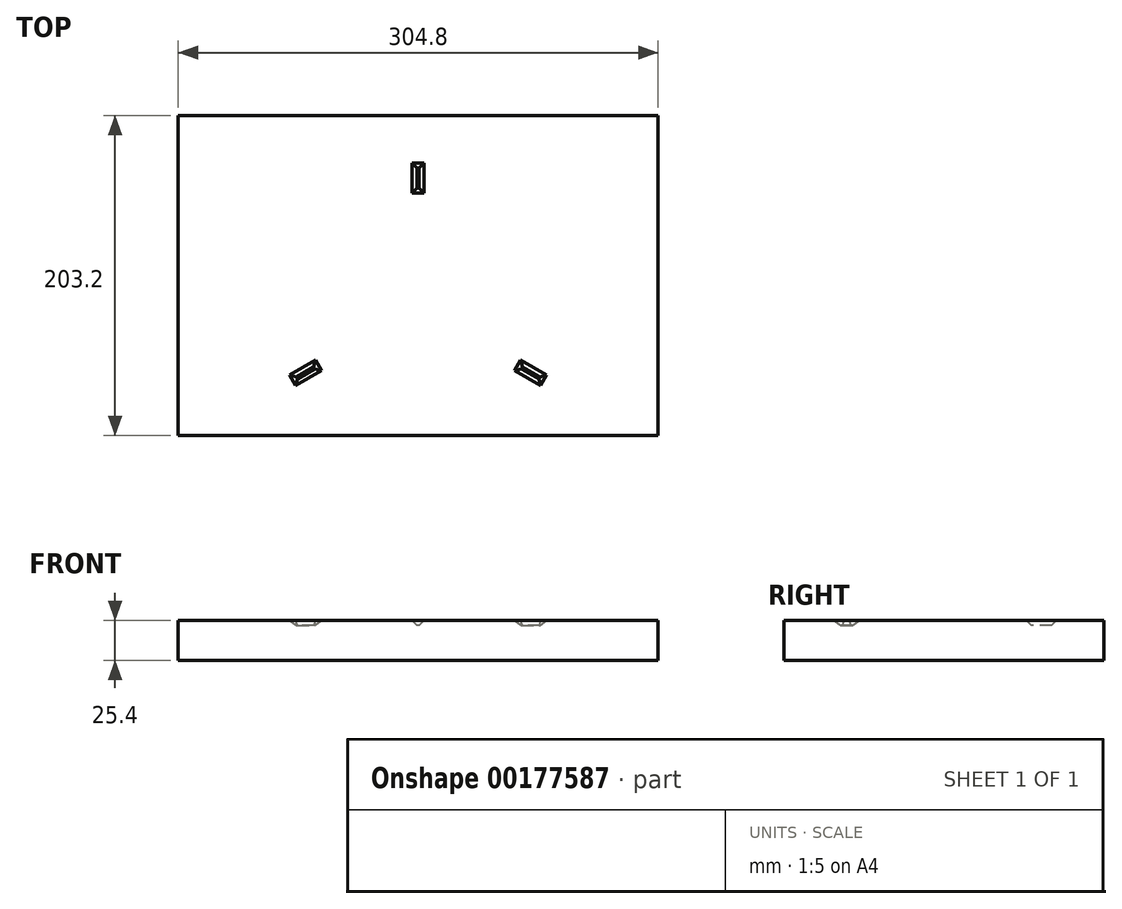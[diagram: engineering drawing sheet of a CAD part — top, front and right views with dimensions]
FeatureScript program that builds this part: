
annotation { "Feature Type Name" : "Feature", "Feature Type Description" : "" }
export const myFeature = defineFeature(function(context is Context, id is Id, definition is map)
    precondition{}
    {
        {
            var Q0;
            Q0=qCreatedBy(makeId("Top.planeOp"),FACE);
            var sketch = newSketch(context, id + "F0", { "sketchPlane" : qUnion([Q0])});
            skLineSegment(sketch, "E0.bottom", {"start": v(-152.4, 101.6) * mm, "end": v(152.4, 101.6) * mm});
            skLineSegment(sketch, "E0.top", {"start": v(-152.4, -101.6) * mm, "end": v(152.4, -101.6) * mm});
            skLineSegment(sketch, "E0.left", {"start": v(-152.4, 101.6) * mm, "end": v(-152.4, -101.6) * mm});
            skLineSegment(sketch, "E0.right", {"start": v(152.4, 101.6) * mm, "end": v(152.4, -101.6) * mm});
            skPoint(sketch, "E0.middle", {"position": v(0, 0) * mm});
            skSolve(sketch);
        }
        {
            var Q0;
            Q0 = qSketchRegion(id + "F0", true);
            extrude(context, id + "F1", {"entities" : qUnion([Q0]), "depth" : 25.4 * mm});
        }
        {
            var Q0;
            Q0=makeQuery(id+"F1.opExtrude","CAP_FACE",FACE,{"disambiguationData":[OSD([sQuery(id+"F0.wireOp",EDGE,"E0.bottom"),sQuery(id+"F0.wireOp",EDGE,"E0.top"),sQuery(id+"F0.wireOp",EDGE,"E0.left"),sQuery(id+"F0.wireOp",EDGE,"E0.right")])],"isStart":false});
            var sketch = newSketch(context, id + "F2", { "sketchPlane" : qUnion([Q0])});
            skLineSegment(sketch, "E1", {"start": v(0, 52.39) * mm, "end": v(0, 71.44) * mm, "construction": true});
            skLineSegment(sketch, "E2", {"start": v(-79.74, -66.67) * mm, "end": v(-63.24, -57.15) * mm, "construction": true});
            skLineSegment(sketch, "E3", {"start": v(79.74, -66.67) * mm, "end": v(63.24, -57.15) * mm, "construction": true});
            skLineSegment(sketch, "E4", {"start": v(0, -61.91) * mm, "end": v(0, 61.91) * mm, "construction": true});
            skLineSegment(sketch, "E5", {"start": v(-71.5, -61.91) * mm, "end": v(71.5, -61.91) * mm, "construction": true});
            skPoint(sketch, "E6.startSnap0", {"position": v(0, -61.91) * mm});
            skCircle(sketch, "E7", {"center": v(0, -20.64) * mm, "radius": 82.55 * mm, "construction": true});
            skLineSegment(sketch, "E8.0.left", {"start": v(-3.8, 52.39) * mm, "end": v(-3.8, 71.44) * mm});
            skLineSegment(sketch, "E8.0.right", {"start": v(3.81, 52.39) * mm, "end": v(3.8, 71.44) * mm});
            skLineSegment(sketch, "E8.1.left", {"start": v(-81.64, -63.38) * mm, "end": v(-65.15, -53.85) * mm});
            skLineSegment(sketch, "E8.1.right", {"start": v(-77.83, -69.97) * mm, "end": v(-61.34, -60.45) * mm});
            skLineSegment(sketch, "E8.2.left", {"start": v(77.83, -69.97) * mm, "end": v(61.34, -60.45) * mm});
            skLineSegment(sketch, "E8.2.right", {"start": v(81.64, -63.38) * mm, "end": v(65.15, -53.85) * mm});
            skLineSegment(sketch, "E9", {"start": v(-71.5, -61.91) * mm, "end": v(0, 61.91) * mm, "construction": true});
            skLineSegment(sketch, "E10", {"start": v(0, 61.91) * mm, "end": v(71.5, -61.91) * mm, "construction": true});
            skLineSegment(sketch, "E11", {"start": v(-3.8, 71.44) * mm, "end": v(3.81, 71.44) * mm});
            skLineSegment(sketch, "E12", {"start": v(3.81, 52.39) * mm, "end": v(-3.8, 52.39) * mm});
            skLineSegment(sketch, "E13", {"start": v(-61.34, -60.45) * mm, "end": v(-65.15, -53.85) * mm});
            skLineSegment(sketch, "E14", {"start": v(-81.64, -63.38) * mm, "end": v(-77.83, -69.97) * mm});
            skLineSegment(sketch, "E15", {"start": v(65.15, -53.85) * mm, "end": v(61.34, -60.45) * mm});
            skLineSegment(sketch, "E16", {"start": v(77.83, -69.97) * mm, "end": v(81.64, -63.38) * mm});
            skSolve(sketch);
        }
        {
            var Q0;
            Q0=makeQuery(id+"F2.imprint","IMPRINT",FACE,{"disambiguationData":[TD([[makeQuery(id+"F2.imprint","IMPRINT",EDGE,{"derivedFrom":sQuery(id+"F2.wireOp",EDGE,"E8.1.left")}),-1.0]])]});
            var Q1;
            Q1=makeQuery(id+"F2.imprint","IMPRINT",FACE,{"disambiguationData":[TD([[makeQuery(id+"F2.imprint","IMPRINT",EDGE,{"derivedFrom":sQuery(id+"F2.wireOp",EDGE,"E8.2.left")}),-1.0]])]});
            var Q2;
            Q2=makeQuery(id+"F2.imprint","IMPRINT",FACE,{"disambiguationData":[TD([[makeQuery(id+"F2.imprint","IMPRINT",EDGE,{"derivedFrom":sQuery(id+"F2.wireOp",EDGE,"E8.0.left")}),-1.0]])]});
            var Q3;
            Q3=sQuery(id+"F2.wireOp",EDGE,"E3");
            extrude(context, id + "F3", {"entities" : qUnion([Q0, Q1, Q2]), "operationType" : NewBodyOperationType.REMOVE, "surfaceEntities" : qUnion([Q3]), "oppositeDirection" : true, "depth" : 3.17 * mm, "hasDraft" : true, "draftAngle" : 45 * degree, "draftPullDirection" : true});
        }
    });
